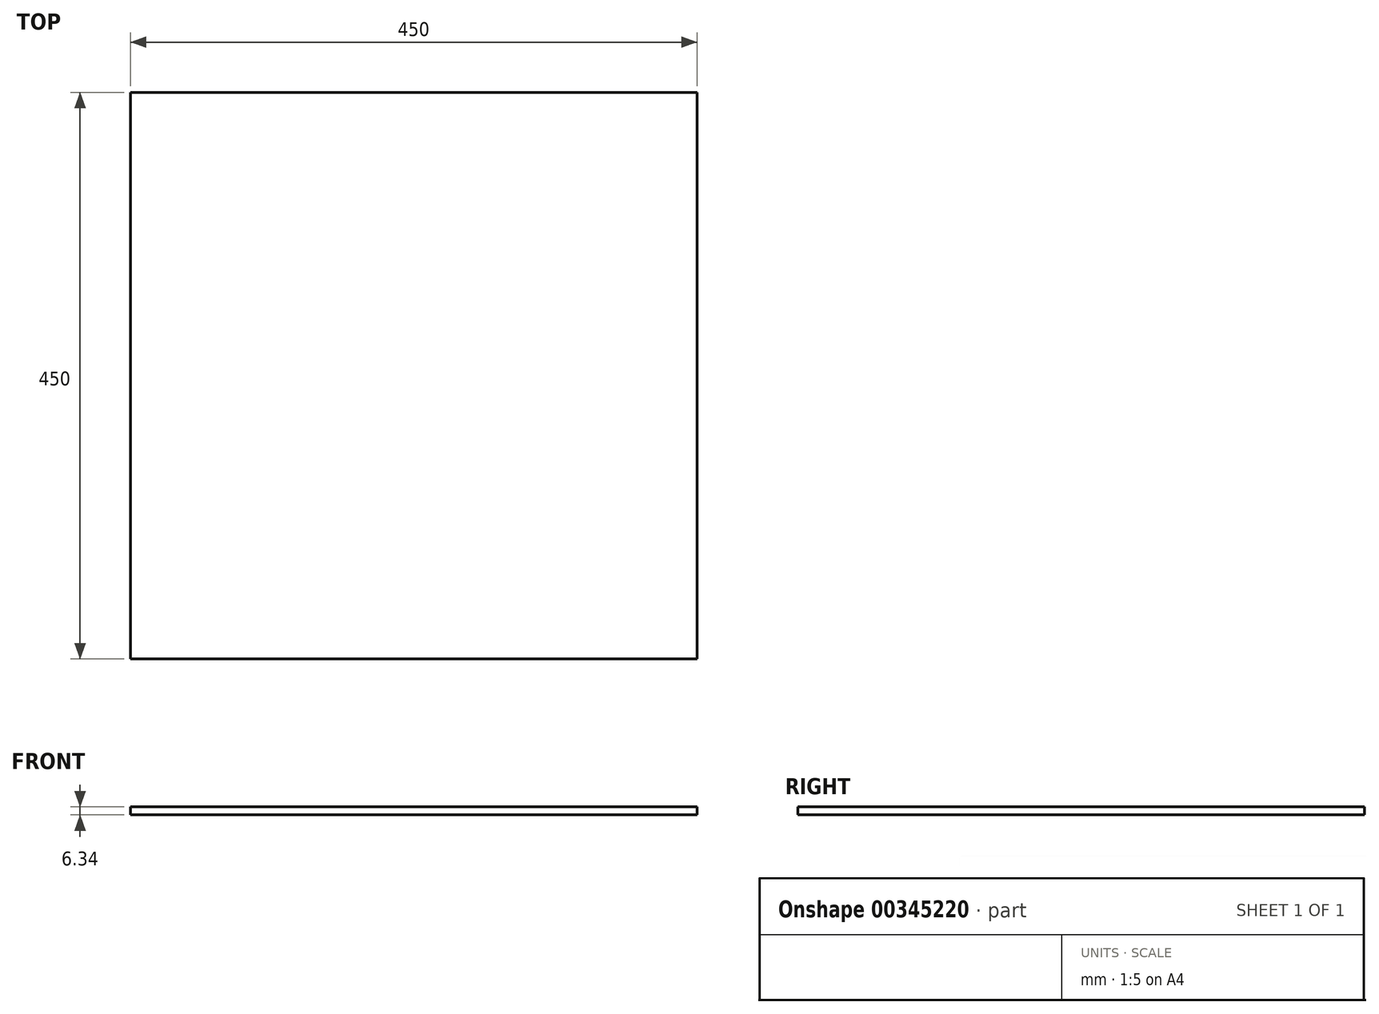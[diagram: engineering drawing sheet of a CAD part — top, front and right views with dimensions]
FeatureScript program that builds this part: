
annotation { "Feature Type Name" : "Feature", "Feature Type Description" : "" }
export const myFeature = defineFeature(function(context is Context, id is Id, definition is map)
    precondition{}
    {
        {
            var Q0;
            Q0=qCreatedBy(makeId("Top.planeOp"),FACE);
            var sketch = newSketch(context, id + "F0", { "sketchPlane" : qUnion([Q0])});
            skLineSegment(sketch, "E0.bottom", {"start": v(0, -95.58) * mm, "end": v(-450, -95.58) * mm});
            skLineSegment(sketch, "E0.top", {"start": v(0, 354.42) * mm, "end": v(-450, 354.42) * mm});
            skLineSegment(sketch, "E0.left", {"start": v(0, -95.58) * mm, "end": v(0, 354.42) * mm});
            skLineSegment(sketch, "E0.right", {"start": v(-450, -95.58) * mm, "end": v(-450, 354.42) * mm});
            skPoint(sketch, "E0.middle", {"position": v(-225, 129.42) * mm});
            skSolve(sketch);
        }
        {
            var Q0;
            Q0 = qSketchRegion(id + "F0", true);
            extrude(context, id + "F1", {"entities" : qUnion([Q0]), "endBound" : BoundingType.SYMMETRIC, "depth" : 6.35 * mm});
        }
    });
